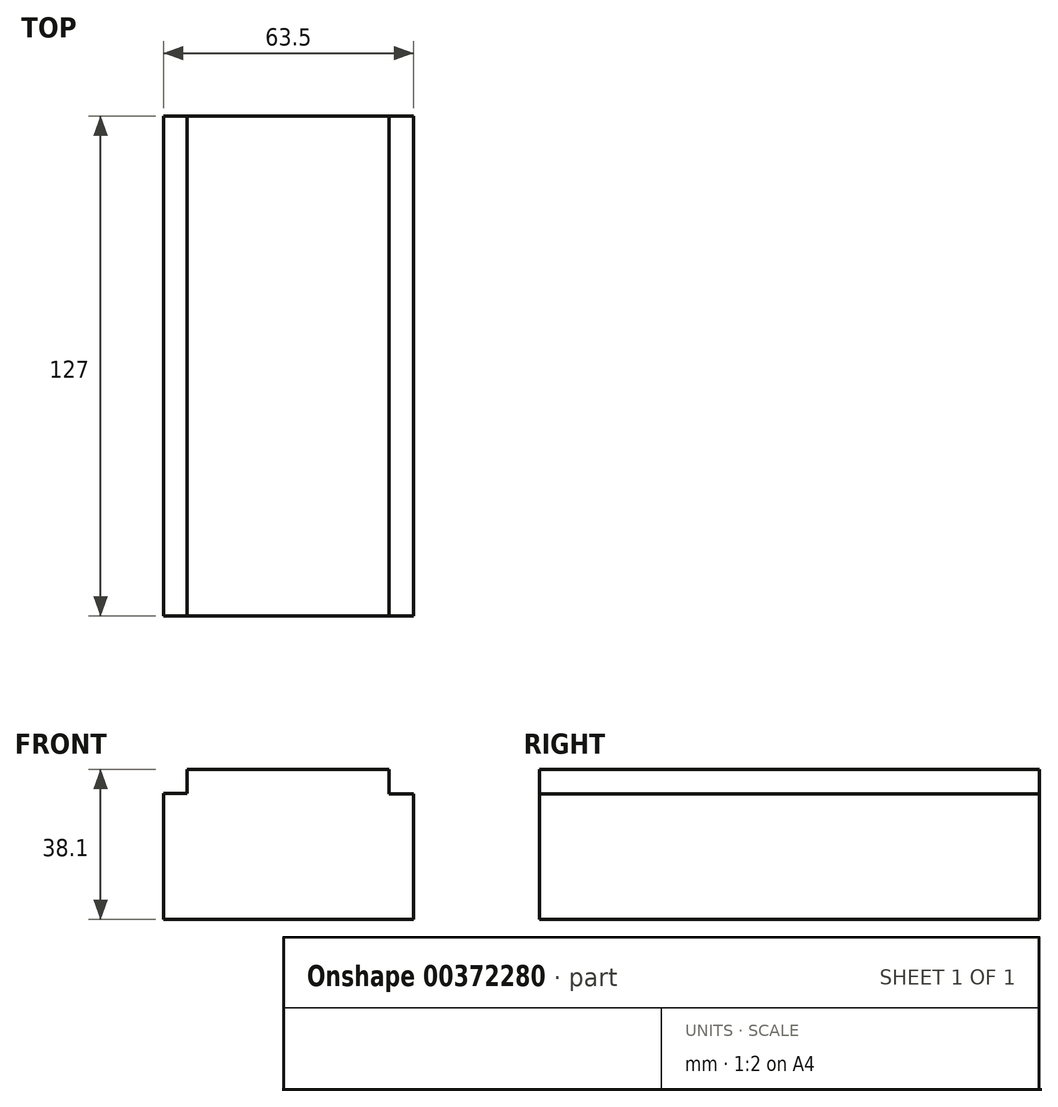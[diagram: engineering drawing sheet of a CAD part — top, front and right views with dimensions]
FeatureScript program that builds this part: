
annotation { "Feature Type Name" : "Feature", "Feature Type Description" : "" }
export const myFeature = defineFeature(function(context is Context, id is Id, definition is map)
    precondition{}
    {
        {
            var Q0;
            Q0=qCreatedBy(makeId("Front.planeOp"),FACE);
            var sketch = newSketch(context, id + "F0", { "sketchPlane" : qUnion([Q0])});
            skLineSegment(sketch, "E0.bottom", {"start": v(-31.75, 19.05) * mm, "end": v(31.75, 19.05) * mm});
            skLineSegment(sketch, "E0.top", {"start": v(-31.75, -19.05) * mm, "end": v(31.75, -19.05) * mm});
            skLineSegment(sketch, "E0.left", {"start": v(-31.75, 19.05) * mm, "end": v(-31.75, -19.05) * mm});
            skLineSegment(sketch, "E0.right", {"start": v(31.75, 19.05) * mm, "end": v(31.75, -19.05) * mm});
            skPoint(sketch, "E0.middle", {"position": v(0, 0) * mm});
            skSolve(sketch);
        }
        {
            var Q0;
            Q0 = qSketchRegion(id + "F0", true);
            extrude(context, id + "F1", {"entities" : qUnion([Q0]), "depth" : 127 * mm});
        }
        {
            var Q0;
            Q0=qCreatedBy(makeId("Front.planeOp"),FACE);
            var sketch = newSketch(context, id + "F2", { "sketchPlane" : qUnion([Q0])});
            skLineSegment(sketch, "E1.bottom", {"start": v(31.9, 19.17) * mm, "end": v(25.54, 19.17) * mm});
            skLineSegment(sketch, "E1.top", {"start": v(31.9, 12.82) * mm, "end": v(25.54, 12.82) * mm});
            skLineSegment(sketch, "E1.left", {"start": v(31.9, 19.17) * mm, "end": v(31.9, 12.82) * mm});
            skLineSegment(sketch, "E1.right", {"start": v(25.54, 19.17) * mm, "end": v(25.54, 12.82) * mm});
            skSolve(sketch);
        }
        {
            var Q0;
            Q0=qCreatedBy(makeId("Front.planeOp"),FACE);
            var sketch = newSketch(context, id + "F3", { "sketchPlane" : qUnion([Q0])});
            skLineSegment(sketch, "E2.bottom", {"start": v(-32.16, 19.25) * mm, "end": v(-25.8, 19.25) * mm});
            skLineSegment(sketch, "E2.top", {"start": v(-32.16, 12.9) * mm, "end": v(-25.8, 12.9) * mm});
            skLineSegment(sketch, "E2.left", {"start": v(-32.16, 19.25) * mm, "end": v(-32.16, 12.9) * mm});
            skLineSegment(sketch, "E2.right", {"start": v(-25.8, 19.25) * mm, "end": v(-25.8, 12.9) * mm});
            skSolve(sketch);
        }
        {
            var Q0;
            Q0 = qSketchRegion(id + "F3", true);
            extrude(context, id + "F4", {"entities" : qUnion([Q0]), "operationType" : NewBodyOperationType.REMOVE, "depth" : 127 * mm});
        }
        {
            var Q0;
            Q0 = qSketchRegion(id + "F2", true);
            extrude(context, id + "F5", {"entities" : qUnion([Q0]), "operationType" : NewBodyOperationType.REMOVE, "oppositeDirection" : true, "depth" : -127 * mm});
        }
    });
